# Revit family: xxxCommercial_Shower_System-American_Standard-TU662213.002
name_source: partatom
category: Plumbing Fixtures
units: mm (PartAtom-declared; Revit-internal decimal feet)

## family parameters
Cut with Voids When Loaded = No
Host = Face
OmniClass Number = 23.45.05.14.17
OmniClass Title = Showers
Part Type = Normal
Room Calculation Point = No
Round Connector Dimension = Use Diameter
Shared = Yes

## types (1)
- TU662.213.002
    1660.236 36" Slide Bar = Yes
    1660.400 In-Line Vacuum Breaker = Yes
    1660.710 FloWise Showerhead = Yes
    1660.766 3-Function Hand Shower with non-positive shut-off = Yes
    2-Way Diverter Valve (R422) = Sold Separately
    8888.035 59" Metal Hose = Yes
    8888.037 Wall Supply = Yes
    ADA Compliant = Yes
    Assembly Code = D2010710
    CEC Compliant = Yes
    CW Connection = Yes
    CWFU = 3
    CalGreen Compliant = Yes
    Cold Water Connection Description = 1/2" NPT Female CW Inlet Connection
    Cold Water Connection Diameter = 1/2"
    Connection Diameter = 1/2"
    Default Elevation = 0"
    Description = Commercial Shower System Trim Kit 1.5 gpm/5.7 Lpm With 36-Inch Slide Bar, Hand Shower and Showerhead
    EPA WaterSense® Certified = Yes
    Finish = Metal-American Standard-002-Polished Chrome
    Flash Rough-In Valve = Sold Separately
    Flow Rate = 1.5 gpm/5.7 Lpm
    HW Connection = Yes
    HWFU = 3
    Height = 78"
    Hot Water Connection Description = 1/2" NPT Female HW Inlet Connection
    Hot Water Connection Diameter = 1/2"
    IAPMO Compliance = These products meets or exceeds ASSE 1016AS ME A112 .18 .1016CSA B12 5 .16AS ME A112 .18 .1CSA B12 5 .1
    Installation Instruction Link = https://americanstandard.box.com
    Installation Type = Wall Mounted
    Manufacturer = American Standard
    Material = Metal-American Standard-002-Polished Chrome
    Model = TU662.213.002
    Outlet Connection Description = 1/2" NPS Male Outlet Connection
    Price = Prices may vary. Please consult Manufacturer Representative for most up-to-date price list.
    Product Documentation Link = https://americanstandard.box.com
    Product Page URL = https://www.americanstandard-us.com
    T342.430 Diverter Trim Kit = Yes
    TU385500WD Reliant3 Valve Only Trim = Yes
    Tempered Water Connection = Yes
    URL = https://www.americanstandard-us.com
    Vent Connection = No
    WFU = 4
    Waste Connection = No

## geometry (parser evidence)
native form markers: Sweep x20
no freeform markers — native parametric forms only
